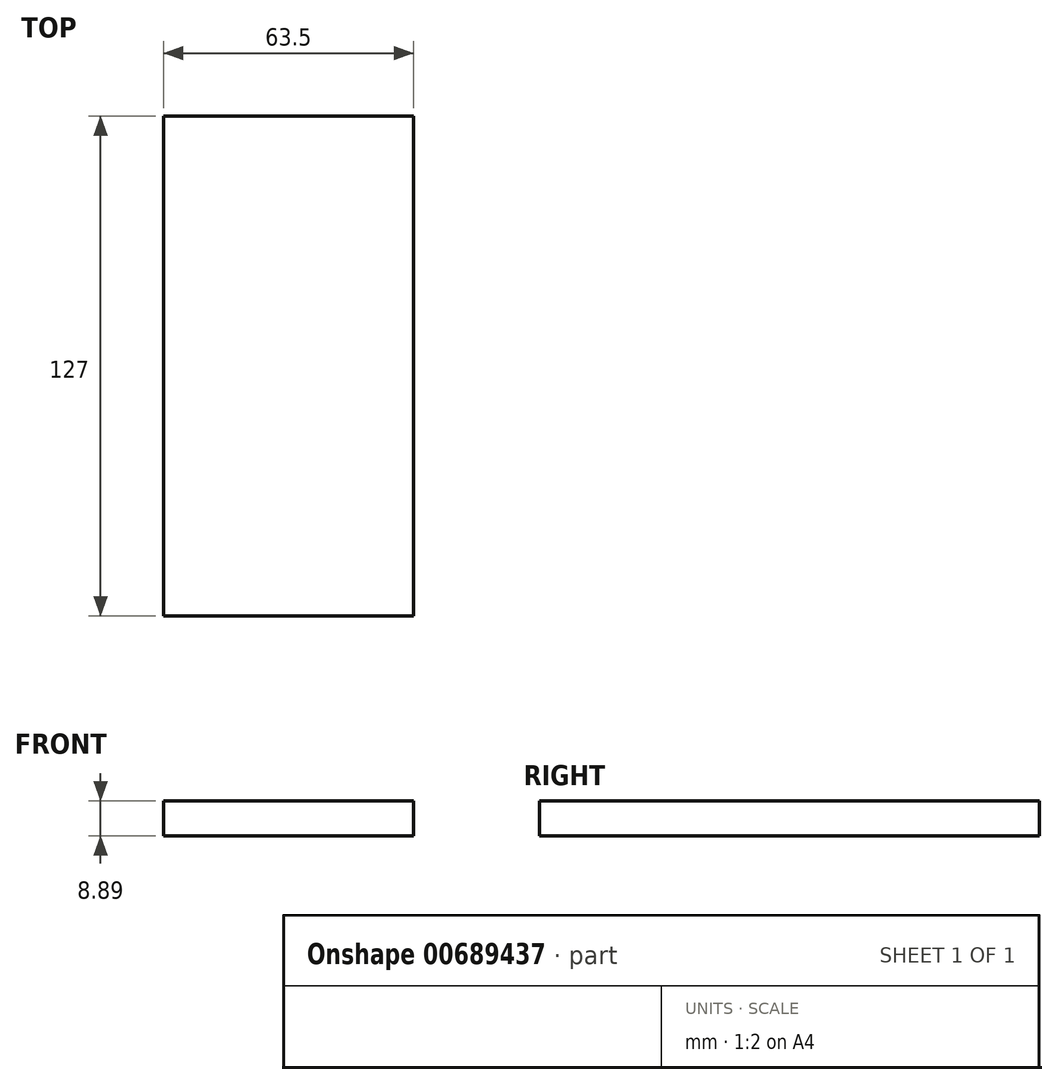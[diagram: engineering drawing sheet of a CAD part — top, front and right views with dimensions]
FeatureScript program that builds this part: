
annotation { "Feature Type Name" : "Feature", "Feature Type Description" : "" }
export const myFeature = defineFeature(function(context is Context, id is Id, definition is map)
    precondition{}
    {
        {
            var Q0;
            Q0=qCreatedBy(makeId("Top.planeOp"),FACE);
            var sketch = newSketch(context, id + "F0", { "sketchPlane" : qUnion([Q0])});
            skLineSegment(sketch, "E0.bottom", {"start": v(-31.75, 63.5) * mm, "end": v(31.75, 63.5) * mm});
            skLineSegment(sketch, "E0.top", {"start": v(-31.75, -63.5) * mm, "end": v(31.75, -63.5) * mm});
            skLineSegment(sketch, "E0.left", {"start": v(-31.75, 63.5) * mm, "end": v(-31.75, -63.5) * mm});
            skLineSegment(sketch, "E0.right", {"start": v(31.75, 63.5) * mm, "end": v(31.75, -63.5) * mm});
            skPoint(sketch, "E0.middle", {"position": v(0, 0) * mm});
            skSolve(sketch);
        }
        {
            var Q0;
            Q0 = qSketchRegion(id + "F0", true);
            extrude(context, id + "F1", {"entities" : qUnion([Q0]), "depth" : 8.9 * mm, "offsetDistance" : 25.4 * mm});
        }
    });
